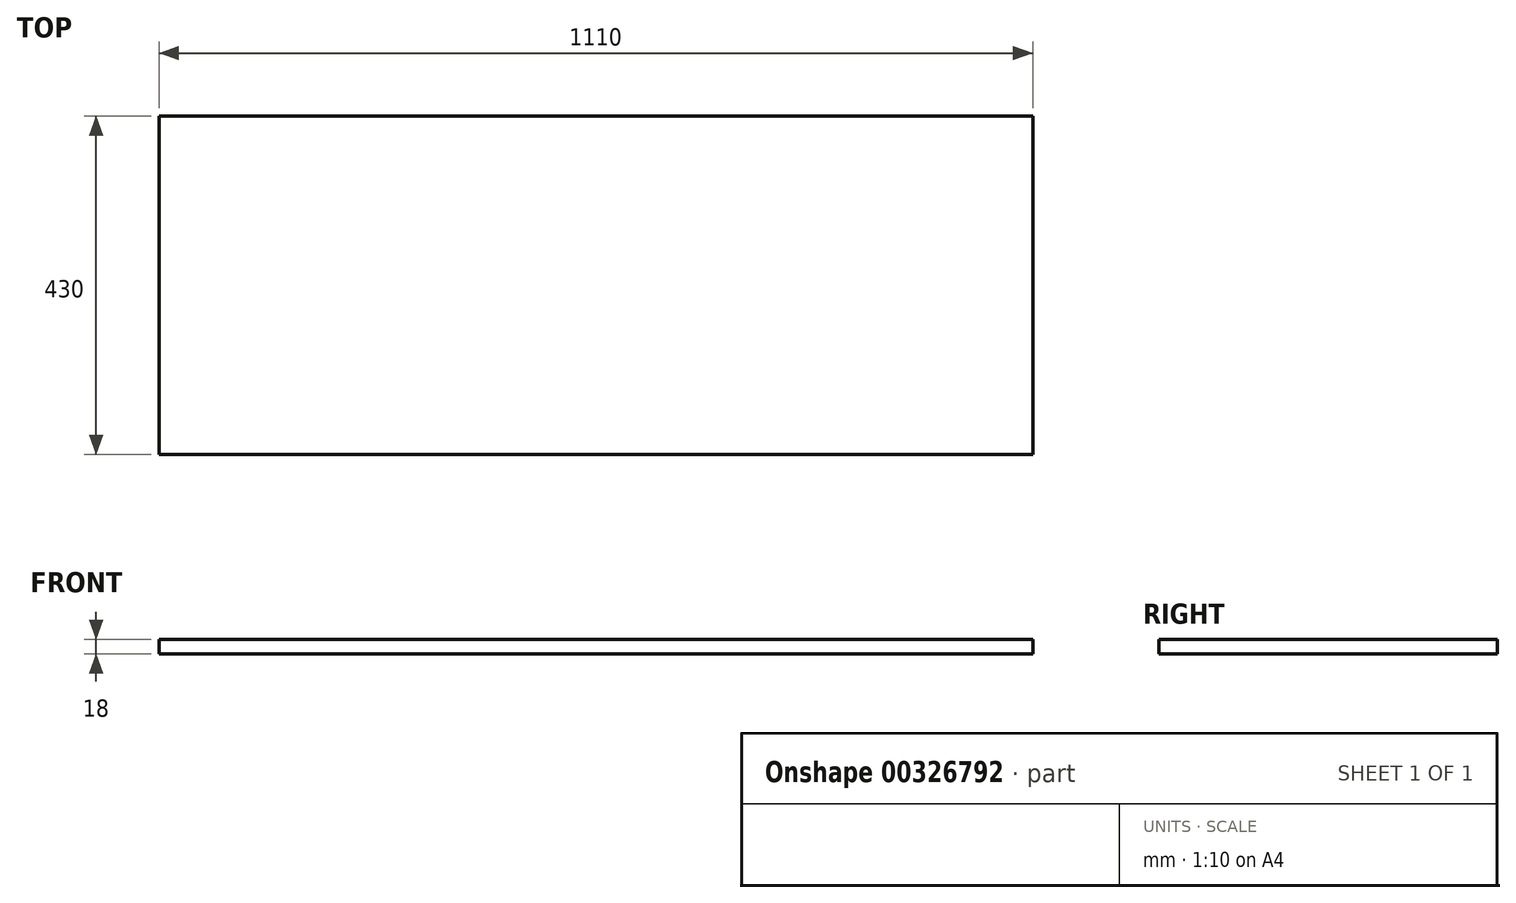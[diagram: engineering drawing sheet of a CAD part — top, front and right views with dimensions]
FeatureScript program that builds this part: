
annotation { "Feature Type Name" : "Feature", "Feature Type Description" : "" }
export const myFeature = defineFeature(function(context is Context, id is Id, definition is map)
    precondition{}
    {
        {
            var Q0;
            Q0=qCreatedBy(makeId("Top.planeOp"),FACE);
            var sketch = newSketch(context, id + "F0", { "sketchPlane" : qUnion([Q0])});
            skLineSegment(sketch, "E0.bottom", {"start": v(0, 0) * mm, "end": v(1110, 0) * mm});
            skLineSegment(sketch, "E0.top", {"start": v(0, 430) * mm, "end": v(1110, 430) * mm});
            skLineSegment(sketch, "E0.left", {"start": v(0, 0) * mm, "end": v(0, 430) * mm});
            skLineSegment(sketch, "E0.right", {"start": v(1110, 0) * mm, "end": v(1110, 430) * mm});
            skSolve(sketch);
        }
        {
            var Q0;
            Q0=qSketchRegion(id+"F0",true);
            extrude(context, id + "F1", {"entities" : qUnion([Q0]), "depth" : 18 * mm});
        }
    });
